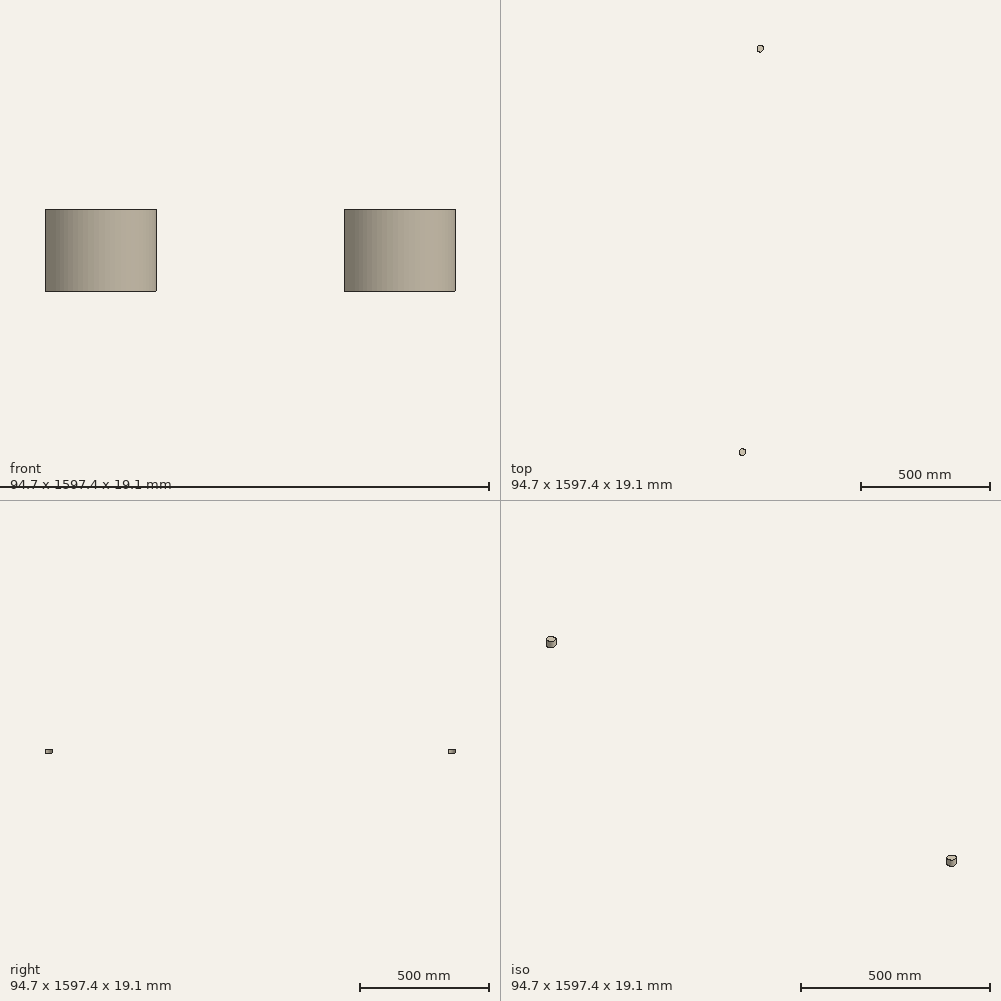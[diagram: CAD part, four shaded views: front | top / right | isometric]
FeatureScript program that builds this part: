
annotation { "Feature Type Name" : "Feature", "Feature Type Description" : "" }
export const myFeature = defineFeature(function(context is Context, id is Id, definition is map)
    precondition{}
    {
        {
            var Q0;
            Q0=qCreatedBy(makeId("Top.planeOp"),FACE);
            var sketch = newSketch(context, id + "F0", { "sketchPlane" : qUnion([Q0])});
            skLineSegment(sketch, "E0", {"start": v(0, 0) * mm, "end": v(304.8, 0) * mm});
            skLineSegment(sketch, "E1", {"start": v(0, 0) * mm, "end": v(-304.8, 0) * mm});
            skLineSegment(sketch, "E2", {"start": v(-304.8, 0) * mm, "end": v(-406.4, 1270) * mm});
            skLineSegment(sketch, "E3", {"start": v(304.8, 0) * mm, "end": v(406.4, 1270) * mm});
            skLineSegment(sketch, "E4.MirrorCS", {"start": v(-373.89, 1676.4) * mm, "end": v(-406.4, 1270) * mm});
            skLineSegment(sketch, "E5.MirrorCS", {"start": v(373.89, 1676.4) * mm, "end": v(406.4, 1270) * mm});
            skLineSegment(sketch, "E6", {"start": v(0, 1676.4) * mm, "end": v(-373.89, 1676.4) * mm});
            skLineSegment(sketch, "E7", {"start": v(0, 1676.4) * mm, "end": v(373.89, 1676.4) * mm});
            skPoint(sketch, "E8.orphan", {"position": v(304.8, 2540) * mm});
            skPoint(sketch, "E9.orphan", {"position": v(-304.8, 2540) * mm});
            skLineSegment(sketch, "E10.0", {"start": v(0, 1625.6) * mm, "end": v(-326.99, 1625.6) * mm});
            skLineSegment(sketch, "E10.1", {"start": v(-326.99, 1625.6) * mm, "end": v(-355.44, 1270) * mm});
            skLineSegment(sketch, "E10.2", {"start": v(0, 1625.6) * mm, "end": v(326.99, 1625.6) * mm});
            skLineSegment(sketch, "E10.3", {"start": v(-257.9, 50.8) * mm, "end": v(-355.44, 1270) * mm});
            skLineSegment(sketch, "E10.4", {"start": v(326.99, 1625.6) * mm, "end": v(355.44, 1270) * mm});
            skLineSegment(sketch, "E10.5", {"start": v(257.9, 50.8) * mm, "end": v(355.44, 1270) * mm});
            skLineSegment(sketch, "E10.6", {"start": v(0, 50.8) * mm, "end": v(257.9, 50.8) * mm});
            skLineSegment(sketch, "E10.7", {"start": v(0, 50.8) * mm, "end": v(-257.9, 50.8) * mm});
            skSolve(sketch);
        }
        {
            var Q0;
            Q0=makeQuery(id+"F0.imprint","IMPRINT",FACE,{"disambiguationData":[TD([[makeQuery(id+"F0.imprint","IMPRINT",EDGE,{"derivedFrom":sQuery(id+"F0.wireOp",EDGE,"E0")}),1.0]])]});
            extrude(context, id + "F1", {"entities" : qUnion([Q0]), "depth" : 19.05 * mm, "offsetDistance" : 25.4 * mm});
        }
        {
            var Q0;
            Q0=makeQuery(id+"F1.opExtrude","SWEPT_EDGE",EDGE,{"disambiguationData":[OSD([sQuery(id+"F0.wireOp",EDGE,"E1"),sQuery(id+"F0.wireOp",EDGE,"E2")])]});
            var Q1;
            Q1=makeQuery(id+"F1.opExtrude","SWEPT_EDGE",EDGE,{"disambiguationData":[OSD([sQuery(id+"F0.wireOp",EDGE,"E0"),sQuery(id+"F0.wireOp",EDGE,"E3")])]});
            var Q2;
            Q2=makeQuery(id+"F1.opExtrude","SWEPT_EDGE",EDGE,{"disambiguationData":[OSD([sQuery(id+"F0.wireOp",EDGE,"E5.MirrorCS"),sQuery(id+"F0.wireOp",EDGE,"E7")])]});
            var Q3;
            Q3=makeQuery(id+"F1.opExtrude","SWEPT_EDGE",EDGE,{"disambiguationData":[OSD([sQuery(id+"F0.wireOp",EDGE,"E4.MirrorCS"),sQuery(id+"F0.wireOp",EDGE,"E6")])]});
            var Q4;
            Q4=makeQuery(id+"F1.opExtrude","SWEPT_EDGE",EDGE,{"disambiguationData":[OSD([sQuery(id+"F0.wireOp",EDGE,"E10.0"),sQuery(id+"F0.wireOp",EDGE,"E10.1")])]});
            var Q5;
            Q5=makeQuery(id+"F1.opExtrude","SWEPT_EDGE",EDGE,{"disambiguationData":[OSD([sQuery(id+"F0.wireOp",EDGE,"E10.2"),sQuery(id+"F0.wireOp",EDGE,"E10.4")])]});
            var Q6;
            Q6=makeQuery(id+"F1.opExtrude","SWEPT_EDGE",EDGE,{"disambiguationData":[OSD([sQuery(id+"F0.wireOp",EDGE,"E10.3"),sQuery(id+"F0.wireOp",EDGE,"E10.7")])]});
            var Q7;
            Q7=makeQuery(id+"F1.opExtrude","SWEPT_EDGE",EDGE,{"disambiguationData":[OSD([sQuery(id+"F0.wireOp",EDGE,"E10.5"),sQuery(id+"F0.wireOp",EDGE,"E10.6")])]});
            fillet(context, id + "F2", {"entities" : qUnion([Q0, Q1, Q2, Q3, Q4, Q5, Q6, Q7]), "radius" : 101.6 * mm, "tangentPropagation" : true, "allowEdgeOverflow" : false});
        }
        {
            var Q0;
            Q0=makeQuery(id+"F1.opExtrude","SWEPT_EDGE",EDGE,{"disambiguationData":[OSD([sQuery(id+"F0.wireOp",EDGE,"E2"),sQuery(id+"F0.wireOp",EDGE,"E4.MirrorCS")])]});
            var Q1;
            Q1=makeQuery(id+"F1.opExtrude","SWEPT_EDGE",EDGE,{"disambiguationData":[OSD([sQuery(id+"F0.wireOp",EDGE,"E3"),sQuery(id+"F0.wireOp",EDGE,"E5.MirrorCS")])]});
            fillet(context, id + "F3", {"entities" : qUnion([Q0, Q1]), "radius" : 1270 * mm, "tangentPropagation" : true, "allowEdgeOverflow" : false});
        }
        {
            var Q0;
            Q0=makeQuery(id+"F1.opExtrude","CAP_FACE",FACE,{"disambiguationData":[OSD([sQuery(id+"F0.wireOp",EDGE,"E0"),sQuery(id+"F0.wireOp",EDGE,"E1"),sQuery(id+"F0.wireOp",EDGE,"E2"),sQuery(id+"F0.wireOp",EDGE,"E3"),sQuery(id+"F0.wireOp",EDGE,"E4.MirrorCS"),sQuery(id+"F0.wireOp",EDGE,"E5.MirrorCS"),sQuery(id+"F0.wireOp",EDGE,"E6"),sQuery(id+"F0.wireOp",EDGE,"E7"),sQuery(id+"F0.wireOp",EDGE,"E10.0"),sQuery(id+"F0.wireOp",EDGE,"E10.1"),sQuery(id+"F0.wireOp",EDGE,"E10.2"),sQuery(id+"F0.wireOp",EDGE,"E10.3"),sQuery(id+"F0.wireOp",EDGE,"E10.4"),sQuery(id+"F0.wireOp",EDGE,"E10.5"),sQuery(id+"F0.wireOp",EDGE,"E10.6"),sQuery(id+"F0.wireOp",EDGE,"E10.7")])],"isStart":false});
            var sketch = newSketch(context, id + "F4", { "sketchPlane" : qUnion([Q0])});
            skArc(sketch, "E11.0", {"start": v(-312.28, 93.5) * mm, "mid": v(-279.92, 26.95) * mm, "end": v(-211, 0) * mm});
            skLineSegment(sketch, "E12", {"start": v(-279.92, 26.95) * mm, "end": v(-233.02, 77.75) * mm, "construction": true});
            skArc(sketch, "E13.0", {"start": v(-164.1, 50.8) * mm, "mid": v(-233.02, 77.75) * mm, "end": v(-265.38, 144.3) * mm});
            skCircle(sketch, "E14", {"center": v(-256.47, 52.35) * mm, "radius": 12.83 * mm});
            skLineSegment(sketch, "E15", {"start": v(0, 0) * mm, "end": v(0, 50.8) * mm, "construction": true});
            skArc(sketch, "E16.0", {"start": v(-280.1, 1676.4) * mm, "mid": v(-349, 1649.45) * mm, "end": v(-381.37, 1582.9) * mm});
            skArc(sketch, "E16.1", {"start": v(-334.47, 1532.1) * mm, "mid": v(-302.11, 1598.65) * mm, "end": v(-233.2, 1625.6) * mm});
            skLineSegment(sketch, "E17", {"start": v(-349, 1649.45) * mm, "end": v(-291.14, 1702.88) * mm, "construction": true});
            skLineSegment(sketch, "E18", {"start": v(-349, 1649.45) * mm, "end": v(-302.11, 1598.65) * mm, "construction": true});
            skCircle(sketch, "E19", {"center": v(-325.56, 1624.05) * mm, "radius": 12.83 * mm});
            skCircle(sketch, "E20.MirrorC", {"center": v(256.47, 52.35) * mm, "radius": 12.83 * mm});
            skCircle(sketch, "E21.MirrorC", {"center": v(325.56, 1624.05) * mm, "radius": 12.83 * mm});
            skSolve(sketch);
        }
        {
            var Q0;
            Q0=makeQuery(id+"F4.imprint","IMPRINT",FACE,{"disambiguationData":[TD([[makeQuery(id+"F4.imprint","IMPRINT",EDGE,{"derivedFrom":sQuery(id+"F4.wireOp",EDGE,"2d0dbb2f-c875-47bf-88a7-28b73ddf56830.MirrorC")}),-1.0]])]});
            var Q1;
            Q1=makeQuery(id+"F4.imprint","IMPRINT",FACE,{"disambiguationData":[TD([[makeQuery(id+"F4.imprint","IMPRINT",EDGE,{"derivedFrom":sQuery(id+"F4.wireOp",EDGE,"E20.MirrorC")}),-1.0]])]});
            var Q2;
            Q2=makeQuery(id+"F4.imprint","IMPRINT",FACE,{"disambiguationData":[TD([[makeQuery(id+"F4.imprint","IMPRINT",EDGE,{"derivedFrom":sQuery(id+"F4.wireOp",EDGE,"E14")}),1.0]])]});
            var Q3;
            Q3=makeQuery(id+"F4.imprint","IMPRINT",FACE,{"disambiguationData":[TD([[makeQuery(id+"F4.imprint","IMPRINT",EDGE,{"derivedFrom":sQuery(id+"F4.wireOp",EDGE,"E19")}),1.0]])]});
            var Q4;
            Q4=makeQuery(id+"F4.imprint","IMPRINT",FACE,{"disambiguationData":[TD([[makeQuery(id+"F4.imprint","IMPRINT",EDGE,{"derivedFrom":sQuery(id+"F4.wireOp",EDGE,"E21.MirrorC")}),-1.0]])]});
            extrude(context, id + "F5", {"entities" : qUnion([Q0, Q1, Q2, Q3, Q4]), "operationType" : NewBodyOperationType.REMOVE, "endBound" : BoundingType.THROUGH_ALL, "oppositeDirection" : true, "depth" : 25.4 * mm, "offsetDistance" : 25.4 * mm});
        }
    });
